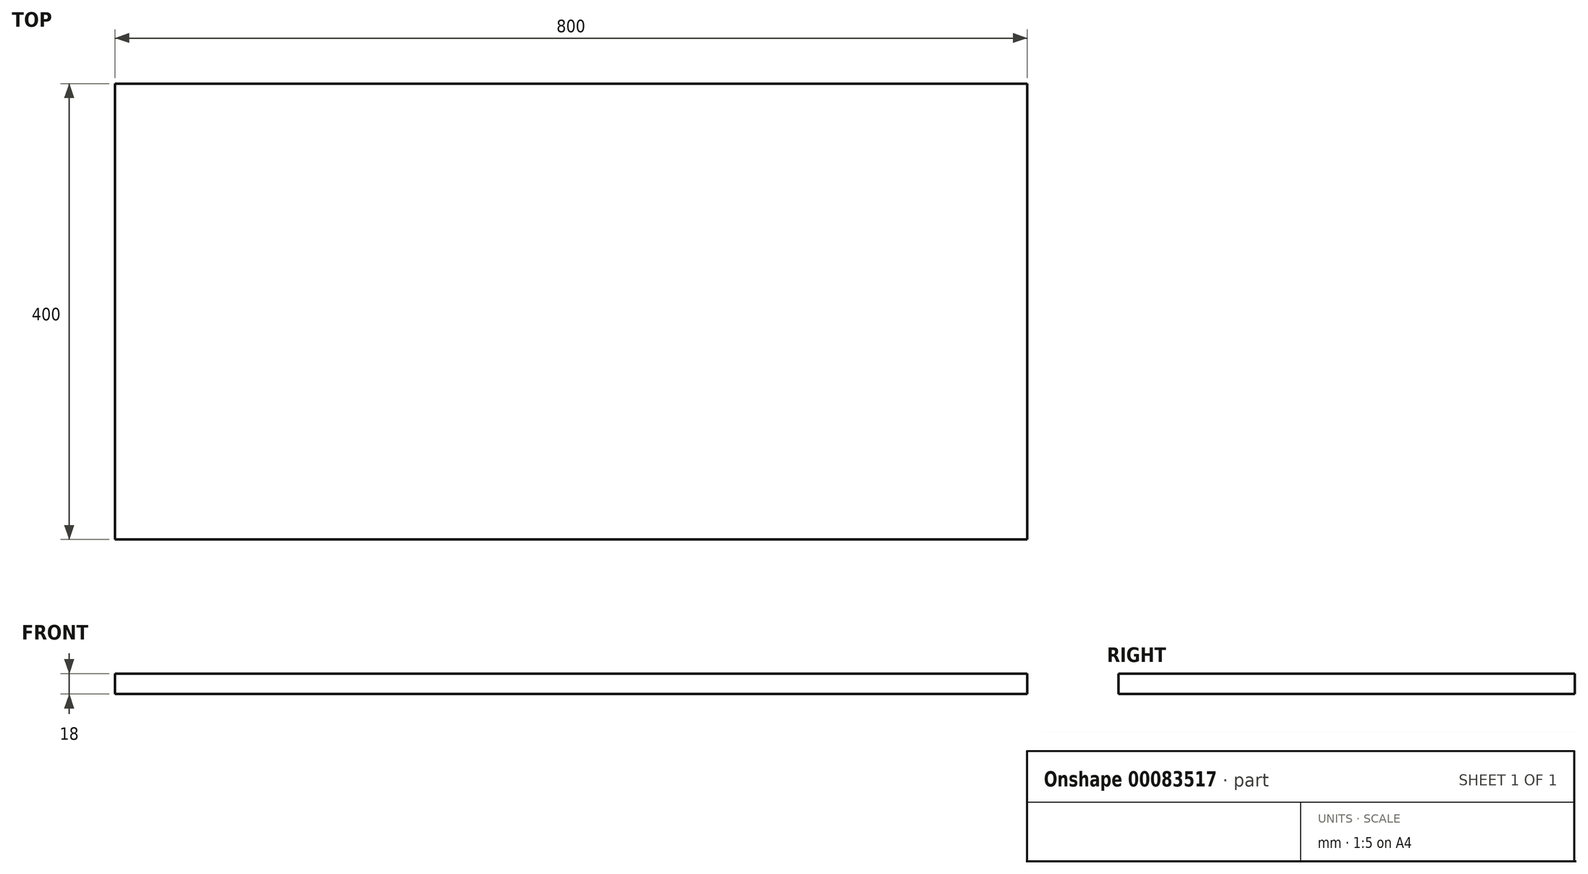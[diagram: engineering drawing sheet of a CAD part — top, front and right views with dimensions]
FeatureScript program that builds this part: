
annotation { "Feature Type Name" : "Feature", "Feature Type Description" : "" }
export const myFeature = defineFeature(function(context is Context, id is Id, definition is map)
    precondition{}
    {
        {
            var Q0;
            Q0=qCreatedBy(makeId("Top.planeOp"),FACE);
            var sketch = newSketch(context, id + "F0", { "sketchPlane" : qUnion([Q0])});
            skLineSegment(sketch, "E0.bottom", {"start": v(-400, 200) * mm, "end": v(400, 200) * mm});
            skLineSegment(sketch, "E0.top", {"start": v(-400, -200) * mm, "end": v(400, -200) * mm});
            skLineSegment(sketch, "E0.left", {"start": v(-400, 200) * mm, "end": v(-400, -200) * mm});
            skLineSegment(sketch, "E0.right", {"start": v(400, 200) * mm, "end": v(400, -200) * mm});
            skPoint(sketch, "E0.middle", {"position": v(0, 0) * mm});
            skSolve(sketch);
        }
        {
            var Q0;
            Q0=makeQuery(id+"F0.imprint","IMPRINT",FACE,{"disambiguationData":[TD([[makeQuery(id+"F0.imprint","IMPRINT",EDGE,{"derivedFrom":sQuery(id+"F0.wireOp",EDGE,"E0.bottom")}),-1.0]])]});
            extrude(context, id + "F1", {"entities" : qUnion([Q0]), "depth" : 18 * mm});
        }
    });
